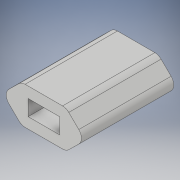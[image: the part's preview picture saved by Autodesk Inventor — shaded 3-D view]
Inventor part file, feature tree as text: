
AUTODESK INVENTOR PART (.ipt)
format: ipt  version: 2019 (Build 230136000, 136)  size: 187,392 bytes
history: native  units: mm
features: extrude x3, sketch x3, projected_geometry x2
ambient origin geometry x8: Origin, YZ Plane, XZ Plane, XY Plane, X Axis, Y Axis, Z Axis, Center Point
bodies: Solid1 (feature_tree)
feature tree (8):
  extrude  "Extrusion1"  Depth=20.0mm TaperAngle=0.0deg
  extrude  "Extrusion2"  Depth=8.0mm
  extrude  "Extrusion3"  Depth=2.0mm TaperAngle=0.0deg
  sketch  "Sketch1"  dims[d0=0.5mm d1=2.0mm d2=20.0mm d3=0.0mm]
  sketch  "Sketch2"  dims[d4=16.0mm d5=8.0mm]
  projected_geometry  "Projected Loop1"
  sketch  "Sketch3"  dims[d6=2.0mm d7=0.0mm d8=25.0mm d9=0.0mm]
  projected_geometry  "Projected Loop2"
